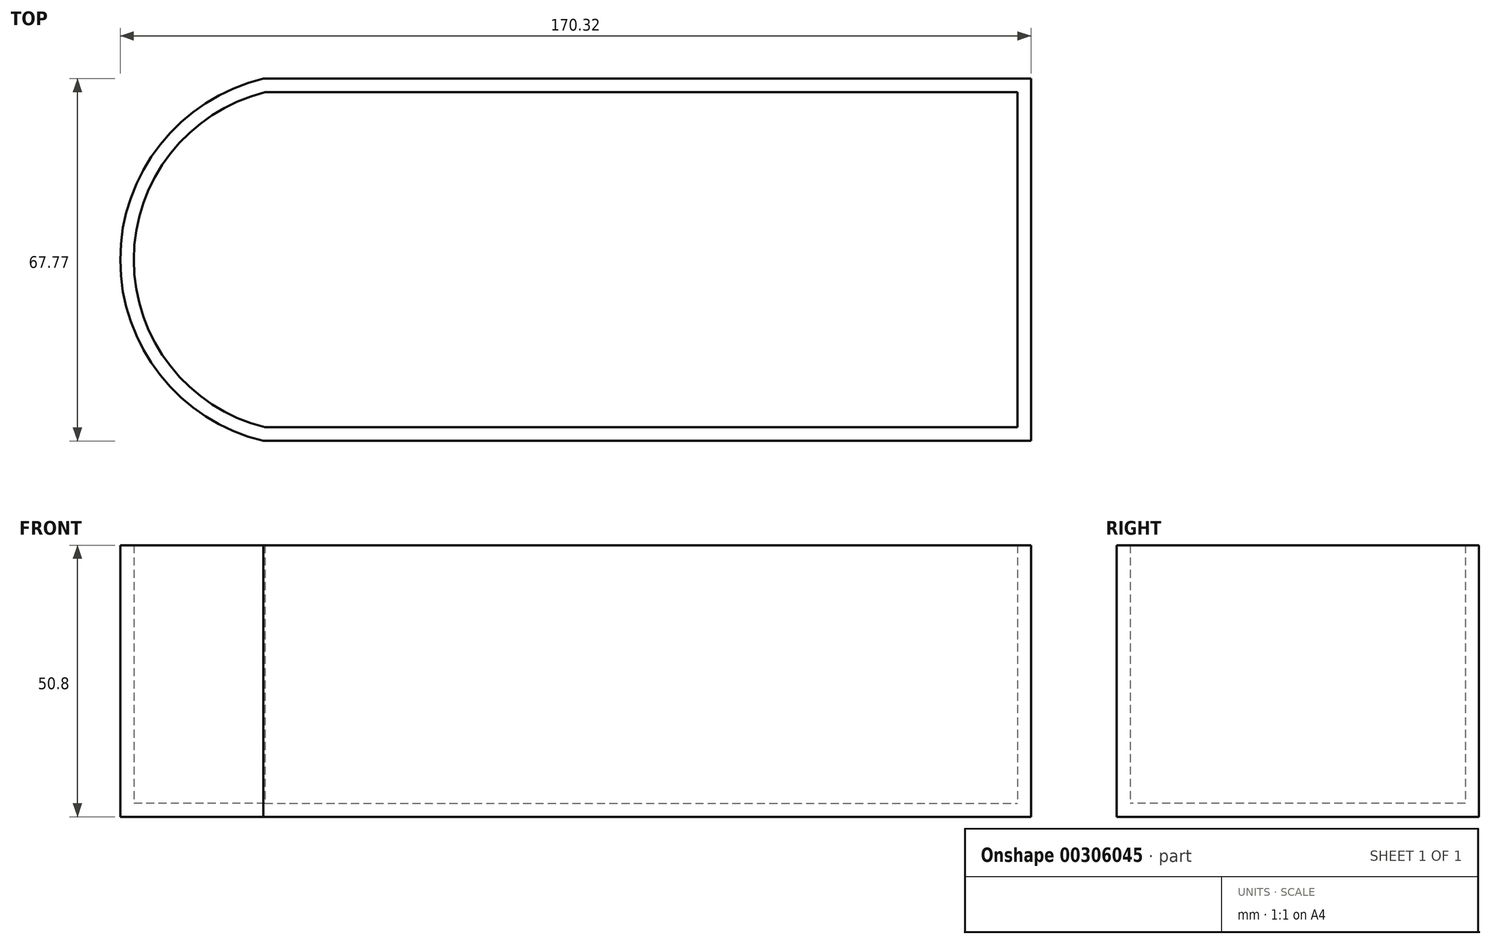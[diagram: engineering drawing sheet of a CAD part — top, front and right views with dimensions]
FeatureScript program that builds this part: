
annotation { "Feature Type Name" : "Feature", "Feature Type Description" : "" }
export const myFeature = defineFeature(function(context is Context, id is Id, definition is map)
    precondition{}
    {
        {
            var Q0;
            Q0=qCreatedBy(makeId("Top.planeOp"),FACE);
            var sketch = newSketch(context, id + "F0", { "sketchPlane" : qUnion([Q0])});
            skLineSegment(sketch, "E0", {"start": v(-72.22, 17.39) * mm, "end": v(71.33, 17.39) * mm});
            skLineSegment(sketch, "E1", {"start": v(71.33, 17.39) * mm, "end": v(71.33, -50.38) * mm});
            skLineSegment(sketch, "E2", {"start": v(71.33, -50.38) * mm, "end": v(-72.22, -50.38) * mm});
            skArc(sketch, "E3", {"start": v(-72.22, 17.39) * mm, "mid": v(-99, -16.5) * mm, "end": v(-72.22, -50.38) * mm});
            skSolve(sketch);
        }
        {
            var Q0;
            Q0 = qSketchRegion(id + "F0", true);
            extrude(context, id + "F1", {"entities" : qUnion([Q0]), "depth" : 50.8 * mm});
        }
        {
            var Q0;
            Q0=makeQuery(id+"F1.opExtrude","CAP_FACE",FACE,{"disambiguationData":[OSD([sQuery(id+"F0.wireOp",EDGE,"E0"),sQuery(id+"F0.wireOp",EDGE,"E1"),sQuery(id+"F0.wireOp",EDGE,"E2"),sQuery(id+"F0.wireOp",EDGE,"E3")])],"isStart":false});
            shell(context, id + "F2", {"entities" : qUnion([Q0]), "thickness" : 2.54 * mm});
        }
    });
